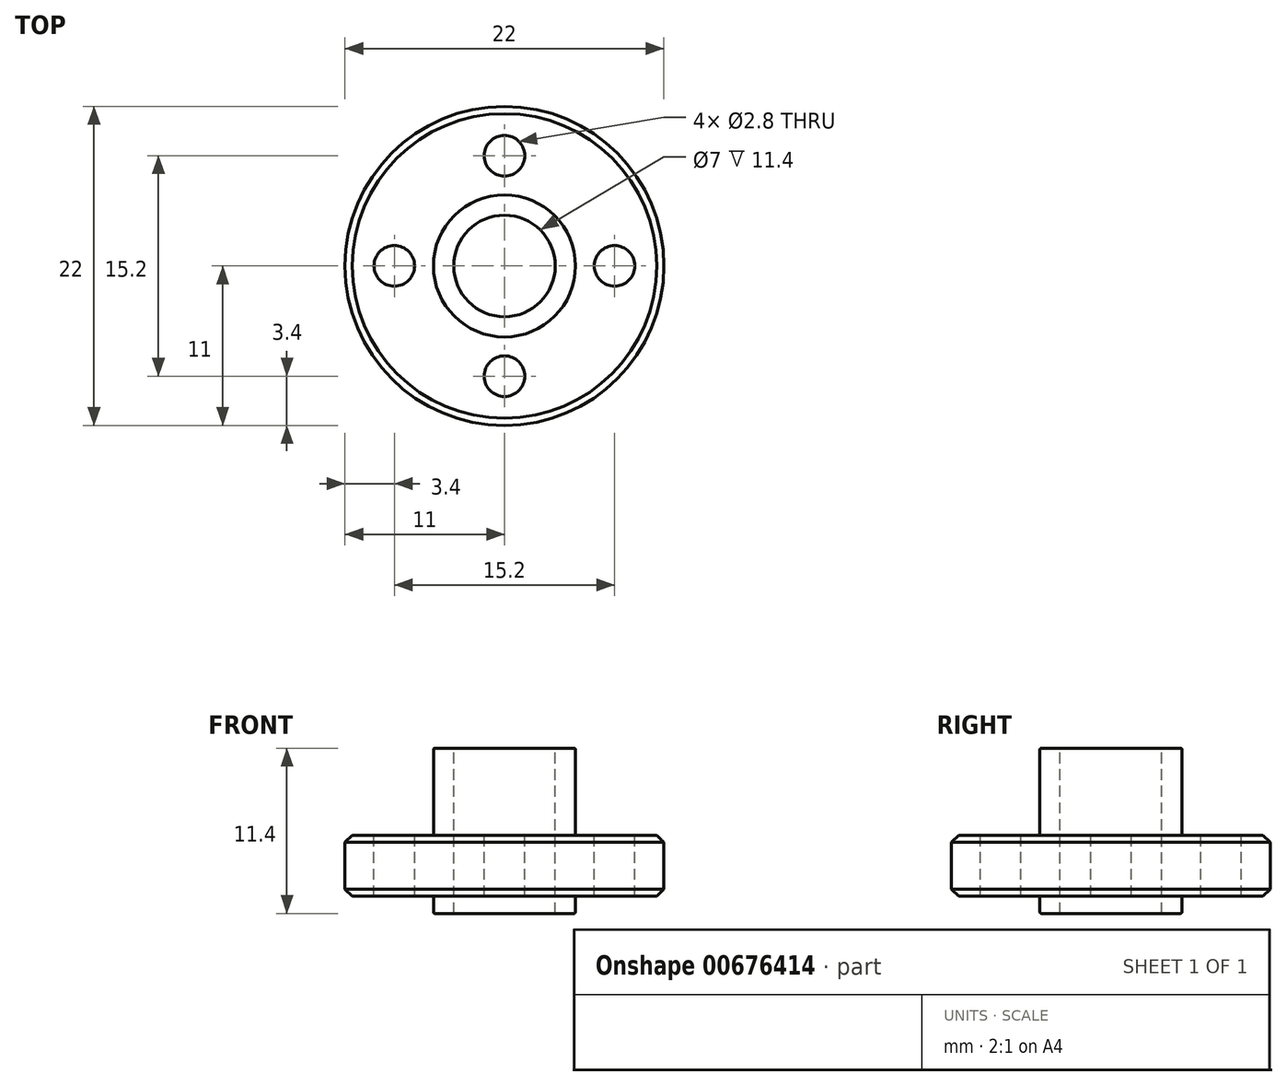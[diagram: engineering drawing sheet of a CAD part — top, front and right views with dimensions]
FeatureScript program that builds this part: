
annotation { "Feature Type Name" : "Feature", "Feature Type Description" : "" }
export const myFeature = defineFeature(function(context is Context, id is Id, definition is map)
    precondition{}
    {
        {
            var Q0;
            Q0=qCreatedBy(makeId("Top.planeOp"),FACE);
            var sketch = newSketch(context, id + "F0", { "sketchPlane" : qUnion([Q0])});
            skCircle(sketch, "E0", {"center": v(0, 0) * mm, "radius": 4.9 * mm});
            skCircle(sketch, "E1", {"center": v(0, 0) * mm, "radius": 11 * mm});
            skLineSegment(sketch, "E2", {"start": v(0, 11) * mm, "end": v(0, -11) * mm, "construction": true});
            skLineSegment(sketch, "E3", {"start": v(-11, 0) * mm, "end": v(11, 0) * mm, "construction": true});
            skCircle(sketch, "E4", {"center": v(0, 7.6) * mm, "radius": 1.4 * mm});
            skCircle(sketch, "E5", {"center": v(7.6, 0) * mm, "radius": 1.4 * mm});
            skCircle(sketch, "E6", {"center": v(0, -7.6) * mm, "radius": 1.4 * mm});
            skCircle(sketch, "E7", {"center": v(-7.6, 0) * mm, "radius": 1.4 * mm});
            skCircle(sketch, "E8", {"center": v(0, 0) * mm, "radius": 3.5 * mm});
            skCircle(sketch, "E9", {"center": v(0, 0) * mm, "radius": 7.6 * mm, "construction": true});
            skSolve(sketch);
        }
        {
            var Q0;
            Q0=makeQuery(id+"F0.imprint","IMPRINT",FACE,{"disambiguationData":[TD([[makeQuery(id+"F0.imprint","IMPRINT",EDGE,{"derivedFrom":sQuery(id+"F0.wireOp",EDGE,"E0")}),1.0]])]});
            var Q1;
            Q1=makeQuery(id+"F0.imprint","IMPRINT",FACE,{"disambiguationData":[TD([[makeQuery(id+"F0.imprint","IMPRINT",EDGE,{"derivedFrom":sQuery(id+"F0.wireOp",EDGE,"E0")}),-1.0]])]});
            extrude(context, id + "F1", {"entities" : qUnion([Q0, Q1]), "flatOperationType" : FlatOperationType.REMOVE, "oppositeDirection" : true, "depth" : 4.22 * mm, "offsetDistance" : 25 * mm, "domain" : OperationDomain.MODEL});
        }
        {
            var Q0;
            Q0=makeQuery(id+"F0.imprint","IMPRINT",FACE,{"disambiguationData":[TD([[makeQuery(id+"F0.imprint","IMPRINT",EDGE,{"derivedFrom":sQuery(id+"F0.wireOp",EDGE,"E0")}),1.0]])]});
            extrude(context, id + "F2", {"entities" : qUnion([Q0]), "operationType" : NewBodyOperationType.ADD, "flatOperationType" : FlatOperationType.REMOVE, "oppositeDirection" : true, "depth" : 5.4 * mm, "offsetDistance" : 25 * mm, "hasSecondDirection" : true, "secondDirectionOppositeDirection" : false, "secondDirectionDepth" : 6 * mm, "domain" : OperationDomain.MODEL});
        }
        {
            var Q0;
            Q0=makeQuery(id+"F1.opExtrude","CAP_EDGE",EDGE,{"disambiguationData":[OSD([sQuery(id+"F0.wireOp",EDGE,"E1")])],"isStart":true});
            var Q1;
            Q1=makeQuery(id+"F1.opExtrude","CAP_EDGE",EDGE,{"disambiguationData":[OSD([sQuery(id+"F0.wireOp",EDGE,"E1")])],"isStart":false});
            chamfer(context, id + "F3", {"entities" : qUnion([Q0, Q1]), "width" : 0.5 * mm, "tangentPropagation" : true});
        }
        {
            var Q0;
            Q0=makeQuery(id+"F2.boolean.opBoolean","INTERSECT",EDGE,{"derivedFrom":[makeQuery(id+"F1.opExtrude","CAP_FACE",FACE,{"disambiguationData":[OSD([sQuery(id+"F0.wireOp",EDGE,"E1"),sQuery(id+"F0.wireOp",EDGE,"E4"),sQuery(id+"F0.wireOp",EDGE,"E5"),sQuery(id+"F0.wireOp",EDGE,"E6"),sQuery(id+"F0.wireOp",EDGE,"E7"),sQuery(id+"F0.wireOp",EDGE,"E8")])],"isStart":true}),makeQuery(id+"F2.opExtrude","SWEPT_FACE",FACE,{"disambiguationData":[OSD([sQuery(id+"F0.wireOp",EDGE,"E0")])]})]});
            var Q1;
            Q1=makeQuery(id+"F2.opExtrude","CAP_EDGE",EDGE,{"disambiguationData":[OSD([sQuery(id+"F0.wireOp",EDGE,"E0")])],"isStart":true});
            var Q2;
            Q2=makeQuery(id+"F2.boolean.opBoolean","INTERSECT",EDGE,{"derivedFrom":[makeQuery(id+"F1.opExtrude","CAP_FACE",FACE,{"disambiguationData":[OSD([sQuery(id+"F0.wireOp",EDGE,"E1"),sQuery(id+"F0.wireOp",EDGE,"E4"),sQuery(id+"F0.wireOp",EDGE,"E5"),sQuery(id+"F0.wireOp",EDGE,"E6"),sQuery(id+"F0.wireOp",EDGE,"E7"),sQuery(id+"F0.wireOp",EDGE,"E8")])],"isStart":false}),makeQuery(id+"F2.opExtrude","SWEPT_FACE",FACE,{"disambiguationData":[OSD([sQuery(id+"F0.wireOp",EDGE,"E0")])]})]});
            var Q3;
            Q3=makeQuery(id+"F2.opExtrude","CAP_EDGE",EDGE,{"disambiguationData":[OSD([sQuery(id+"F0.wireOp",EDGE,"E0")])],"isStart":false});
            fillet(context, id + "F4", {"entities" : qUnion([Q0, Q1, Q2, Q3]), "radius" : 0.1 * mm, "tangentPropagation" : true, "defaultsChanged" : false, "allowEdgeOverflow" : false, "vertexSettings" : []});
        }
    });
